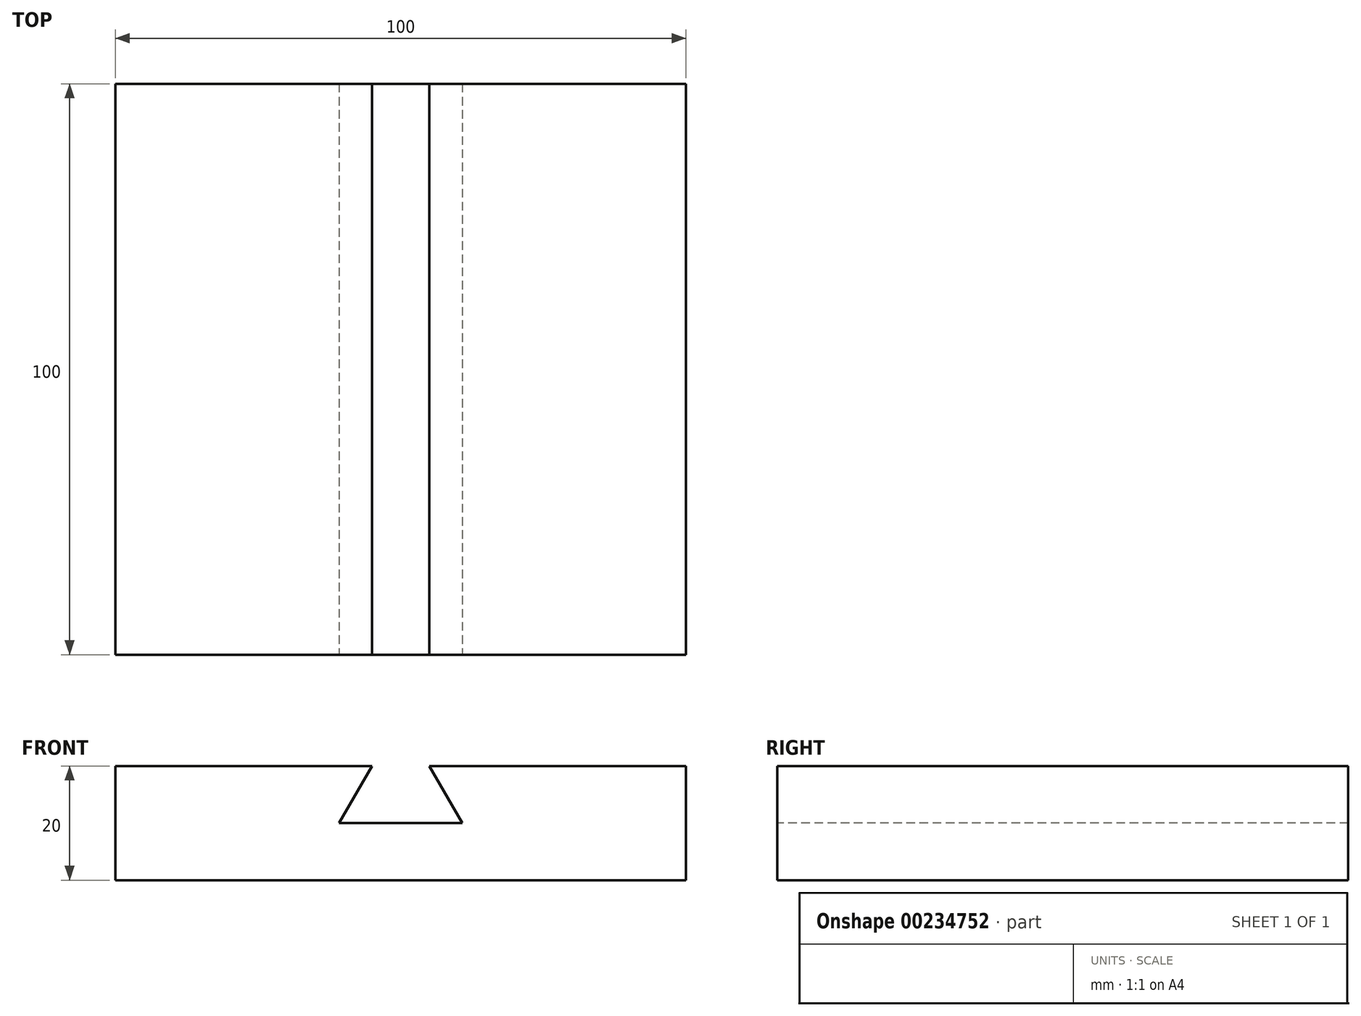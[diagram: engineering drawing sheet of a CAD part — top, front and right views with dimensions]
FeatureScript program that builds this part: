
annotation { "Feature Type Name" : "Feature", "Feature Type Description" : "" }
export const myFeature = defineFeature(function(context is Context, id is Id, definition is map)
    precondition{}
    {
        {
            var Q0;
            Q0=qCreatedBy(makeId("Top.planeOp"),FACE);
            var sketch = newSketch(context, id + "F0", { "sketchPlane" : qUnion([Q0])});
            skLineSegment(sketch, "E0.bottom", {"start": v(50, 50) * mm, "end": v(-50, 50) * mm});
            skLineSegment(sketch, "E0.top", {"start": v(50, -50) * mm, "end": v(-50, -50) * mm});
            skLineSegment(sketch, "E0.left", {"start": v(50, 50) * mm, "end": v(50, -50) * mm});
            skLineSegment(sketch, "E0.right", {"start": v(-50, 50) * mm, "end": v(-50, -50) * mm});
            skPoint(sketch, "E0.middle", {"position": v(0, 0) * mm});
            skSolve(sketch);
        }
        {
            var Q0;
            Q0 = qSketchRegion(id + "F0", true);
            extrude(context, id + "F1", {"entities" : qUnion([Q0]), "oppositeDirection" : true, "depth" : 20 * mm});
        }
        {
            var Q0;
            Q0=makeQuery(id+"F1.opExtrude","SWEPT_FACE",FACE,{"disambiguationData":[OSD([sQuery(id+"F0.wireOp",EDGE,"E0.top")])]});
            var sketch = newSketch(context, id + "F2", { "sketchPlane" : qUnion([Q0])});
            skLineSegment(sketch, "E1", {"start": v(5, 0) * mm, "end": v(10.77, -10) * mm});
            skLineSegment(sketch, "E2", {"start": v(10.77, -10) * mm, "end": v(-10.77, -10) * mm});
            skLineSegment(sketch, "E3", {"start": v(-10.77, -10) * mm, "end": v(-5, 0) * mm});
            skLineSegment(sketch, "E4", {"start": v(-5, 0) * mm, "end": v(-5, 5) * mm});
            skLineSegment(sketch, "E5", {"start": v(-5, 5) * mm, "end": v(5, 5) * mm});
            skLineSegment(sketch, "E6", {"start": v(5, 5) * mm, "end": v(5, 0) * mm});
            skSolve(sketch);
        }
        {
            var Q0;
            Q0 = qSketchRegion(id + "F2", true);
            extrude(context, id + "F3", {"entities" : qUnion([Q0]), "operationType" : NewBodyOperationType.REMOVE, "endBound" : BoundingType.THROUGH_ALL, "oppositeDirection" : true, "depth" : 25 * mm});
        }
    });
